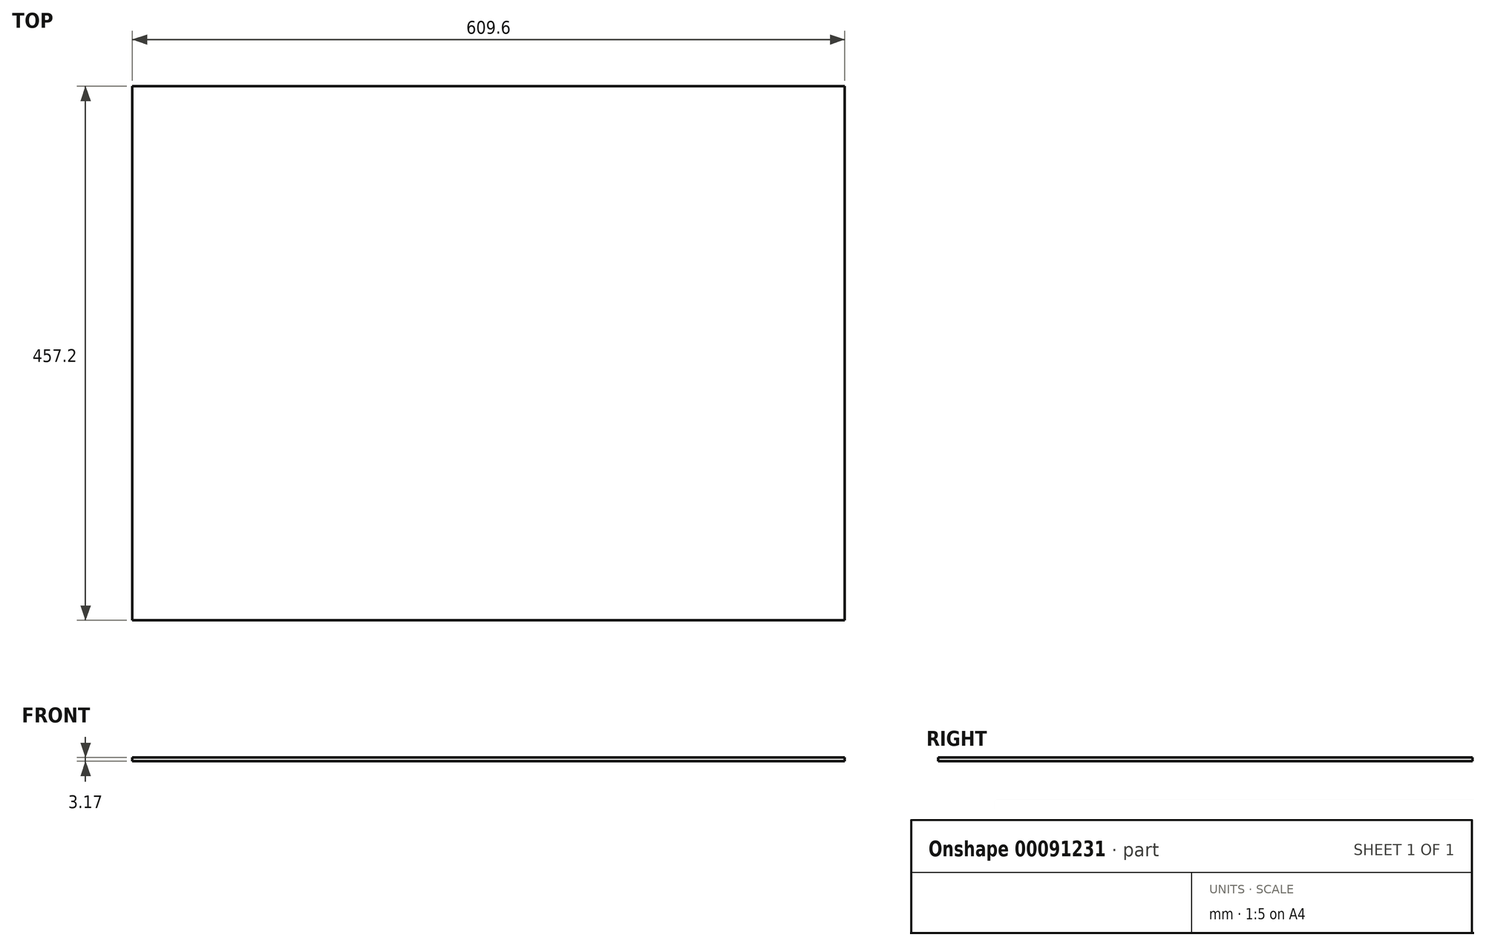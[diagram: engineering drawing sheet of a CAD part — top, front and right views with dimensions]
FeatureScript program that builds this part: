
annotation { "Feature Type Name" : "Feature", "Feature Type Description" : "" }
export const myFeature = defineFeature(function(context is Context, id is Id, definition is map)
    precondition{}
    {
        {
            var Q0;
            Q0=qCreatedBy(makeId("Front.planeOp"),FACE);
            var sketch = newSketch(context, id + "F0", { "sketchPlane" : qUnion([Q0])});
            skLineSegment(sketch, "E0.bottom", {"start": v(0, 0) * mm, "end": v(609.6, 0) * mm});
            skLineSegment(sketch, "E0.top", {"start": v(0, 3.18) * mm, "end": v(609.6, 3.18) * mm});
            skLineSegment(sketch, "E0.left", {"start": v(0, 0) * mm, "end": v(0, 3.18) * mm});
            skLineSegment(sketch, "E0.right", {"start": v(609.6, 0) * mm, "end": v(609.6, 3.18) * mm});
            skSolve(sketch);
        }
        {
            var Q0;
            Q0=makeQuery(id+"F0.imprint","IMPRINT",FACE,{"disambiguationData":[TD([[makeQuery(id+"F0.imprint","IMPRINT",EDGE,{"derivedFrom":sQuery(id+"F0.wireOp",EDGE,"E0.bottom")}),1.0]])]});
            extrude(context, id + "F1", {"entities" : qUnion([Q0]), "depth" : 457.2 * mm});
        }
    });
